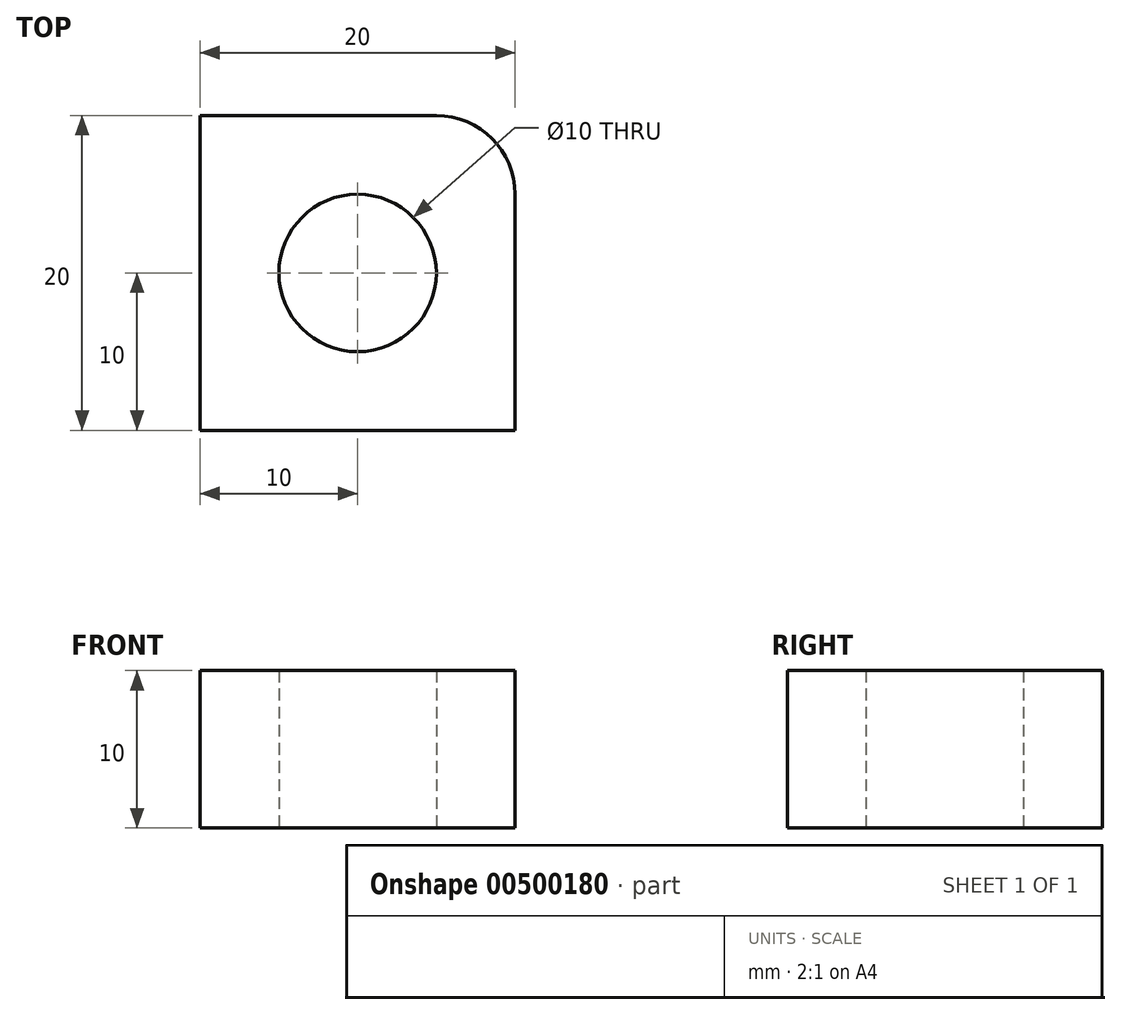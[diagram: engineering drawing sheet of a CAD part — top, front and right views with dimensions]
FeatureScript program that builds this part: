
annotation { "Feature Type Name" : "Feature", "Feature Type Description" : "" }
export const myFeature = defineFeature(function(context is Context, id is Id, definition is map)
    precondition{}
    {
        {
            var Q0;
            Q0=qCreatedBy(makeId("Top.planeOp"),FACE);
            var sketch = newSketch(context, id + "F0", { "sketchPlane" : qUnion([Q0])});
            skLineSegment(sketch, "E0", {"start": v(0, 0) * mm, "end": v(0, 20) * mm});
            skLineSegment(sketch, "E1", {"start": v(0, 20) * mm, "end": v(20, 20) * mm});
            skLineSegment(sketch, "E2", {"start": v(20, 20) * mm, "end": v(20, 0) * mm});
            skLineSegment(sketch, "E3", {"start": v(20, 0) * mm, "end": v(0, 0) * mm});
            skCircle(sketch, "E4", {"center": v(10, 10) * mm, "radius": 5 * mm});
            skPoint(sketch, "E4.centerSnap0", {"position": v(10, 20) * mm});
            skPoint(sketch, "E4.centerSnap1", {"position": v(0, 10) * mm});
            skSolve(sketch);
        }
        {
            var Q0;
            Q0 = qSketchRegion(id + "F0", true);
            extrude(context, id + "F1", {"entities" : qUnion([Q0]), "depth" : 10 * mm});
        }
        {
            var Q0;
            Q0=makeQuery(id+"F1.opExtrude","SWEPT_EDGE",EDGE,{"disambiguationData":[OSD([sQuery(id+"F0.wireOp",EDGE,"E1"),sQuery(id+"F0.wireOp",EDGE,"E2")])]});
            fillet(context, id + "F2", {"entities" : qUnion([Q0]), "radius" : 5 * mm, "tangentPropagation" : true, "allowEdgeOverflow" : false});
        }
    });
